SOLIDWORKS PART (.sldprt)
format: sldprt  version: not decoded by parser v0  size: 96,768 bytes
history: native  units: mm
features: sketch x4, plane x3, cut_extrude x2, material x1, extrude x1, pattern_circular x1 (+10 scaffold rows collapsed)
feature tree (22):
  scaffold x10  (default folders/planes/origin — collapsed)
  material  "Matériau <non spécifié>"
  plane  "Plan de face"
  plane  "Plan de dessus"
  plane  "Plan de droite"
  sketch  "Esquisse1"  dims[D1=~399.878097mm]
  extrude  "Boss.-Extru.1"  Depth=22mm
  sketch  "Esquisse2"  dims[c1.D1=~14.672692mm c1.D2=5.0mm c2.D1=280.0mm]
  cut_extrude  "Enlèv. mat.-Extru.1"  [1 undecoded]
  sketch  "Esquisse3"
  pattern_circular  "Répétition circulaire1"  Count=4 Angle=90deg
  sketch  "Esquisse4"
  cut_extrude  "Enlèv. mat.-Extru.2"  Depth=5mm
decode coverage: 5 of 8 modeling features carry decoded parameters
note: ~ marks probable driven/reference dimensions
note: 1 parameter value undecoded
note: suppression state not decoded; provenance and decode notes live in map.json
